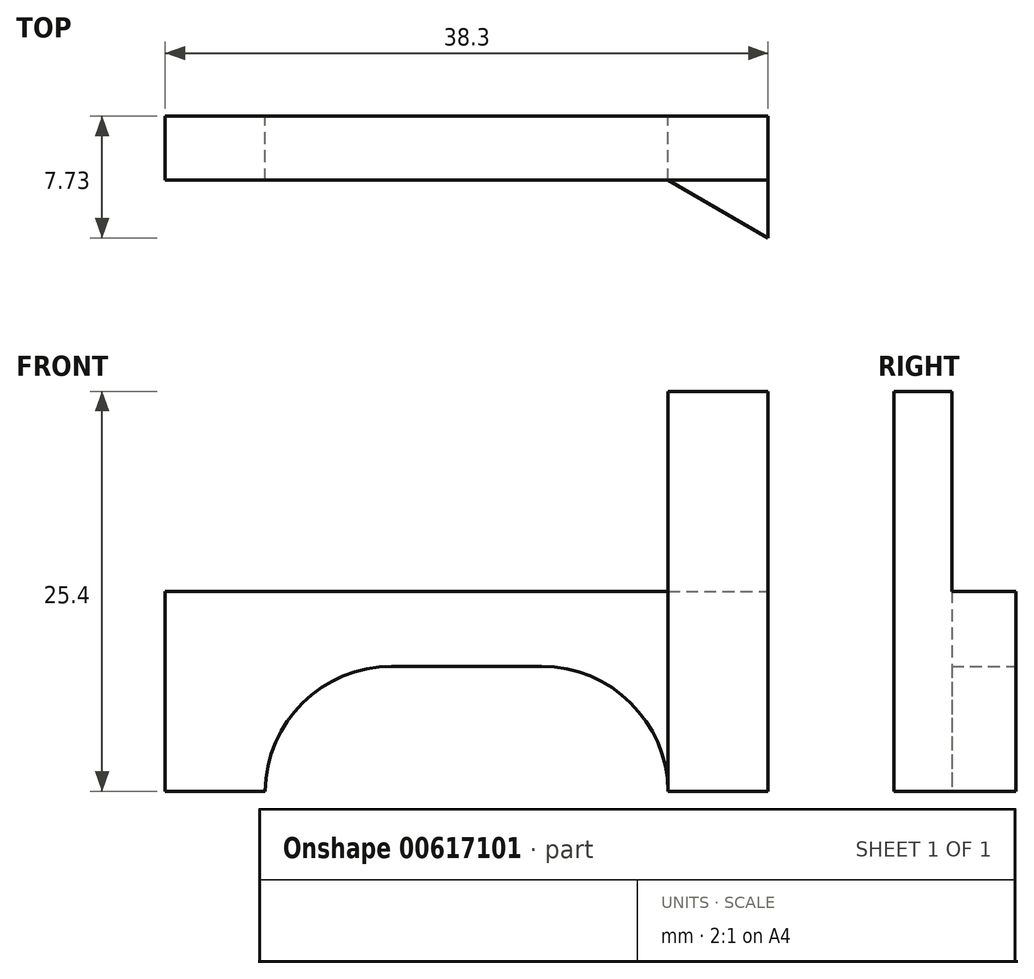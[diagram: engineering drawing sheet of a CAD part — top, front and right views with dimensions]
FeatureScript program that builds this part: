
annotation { "Feature Type Name" : "Feature", "Feature Type Description" : "" }
export const myFeature = defineFeature(function(context is Context, id is Id, definition is map)
    precondition{}
    {
        {
            var Q0;
            Q0=qCreatedBy(makeId("Front.planeOp"),FACE);
            var sketch = newSketch(context, id + "F0", { "sketchPlane" : qUnion([Q0])});
            skLineSegment(sketch, "E0", {"start": v(-31.85, -12.7) * mm, "end": v(-12.8, -12.7) * mm});
            skLineSegment(sketch, "E1", {"start": v(12.8, -12.7) * mm, "end": v(31.85, -12.7) * mm});
            skLineSegment(sketch, "E2", {"start": v(31.85, -12.7) * mm, "end": v(31.85, 0) * mm});
            skLineSegment(sketch, "E3", {"start": v(-4.76, -4.76) * mm, "end": v(0, -4.76) * mm});
            skArc(sketch, "E4", {"start": v(-4.76, -4.76) * mm, "mid": v(-10.4, -7.08) * mm, "end": v(-12.8, -12.7) * mm});
            skArc(sketch, "E5", {"start": v(12.8, -12.7) * mm, "mid": v(10.4, -7.08) * mm, "end": v(4.76, -4.76) * mm});
            skLineSegment(sketch, "E6", {"start": v(-31.85, 0) * mm, "end": v(-31.85, -12.7) * mm});
            skLineSegment(sketch, "E7", {"start": v(0, -4.76) * mm, "end": v(4.76, -4.76) * mm});
            skLineSegment(sketch, "E8", {"start": v(-31.85, 0) * mm, "end": v(0, 0) * mm});
            skLineSegment(sketch, "E9", {"start": v(0, 0) * mm, "end": v(31.85, 0) * mm});
            skSolve(sketch);
        }
        {
            var Q0;
            Q0=qSketchRegion(id+"F0",true);
            extrude(context, id + "F1", {"entities" : qUnion([Q0]), "flatOperationType" : FlatOperationType.REMOVE, "endBound" : BoundingType.SYMMETRIC, "depth" : 4.06 * mm, "offsetDistance" : 25.4 * mm, "domain" : OperationDomain.MODEL});
        }
        {
            var Q0;
            Q0=qCreatedBy(makeId("Top.planeOp"),FACE);
            var sketch = newSketch(context, id + "F2", { "sketchPlane" : qUnion([Q0])});
            skLineSegment(sketch, "E10", {"start": v(12.8, -2.03) * mm, "end": v(19.15, -5.7) * mm});
            skLineSegment(sketch, "E11", {"start": v(19.15, -5.7) * mm, "end": v(19.15, -2.03) * mm});
            skLineSegment(sketch, "E12", {"start": v(19.15, -2.03) * mm, "end": v(12.8, -2.03) * mm});
            skSolve(sketch);
        }
        {
            var Q0;
            Q0 = qSketchRegion(id + "F2", true);
            extrude(context, id + "F3", {"entities" : qUnion([Q0]), "operationType" : NewBodyOperationType.ADD, "flatOperationType" : FlatOperationType.REMOVE, "endBound" : BoundingType.SYMMETRIC, "depth" : 25.4 * mm, "offsetDistance" : 25.4 * mm, "domain" : OperationDomain.MODEL});
        }
        {
            var Q0;
            {var subQ0=sQuery(id+"F2.wireOp",EDGE,"E12");var subQ1=sQuery(id+"F2.wireOp",EDGE,"E11");var subQ2=sQuery(id+"F2.wireOp",EDGE,"E10");Q0=makeQuery(id+"F9uebhGRNWVXSQu_1.1.F3.boolean.opBoolean","MERGE",FACE,{"derivedFrom":[makeQuery(id+"F3.boolean.opBoolean","MERGE",FACE,{"derivedFrom":[makeQuery(id+"F1.opExtrude","SWEPT_FACE",FACE,{"disambiguationData":[OSD([sQuery(id+"F0.wireOp",EDGE,"E1")])]}),makeQuery(id+"F3.opExtrude","CAP_FACE",FACE,{"disambiguationData":[OSD([subQ2,subQ1,subQ0])],"isStart":true})]}),makeQuery(id+"F9uebhGRNWVXSQu_1.1.F3.opExtrude","CAP_FACE",FACE,{"disambiguationData":[OSD([subQ2,subQ1,subQ0])],"isStart":true})]});}
            var sketch = newSketch(context, id + "F4", { "sketchPlane" : qUnion([Q0])});
            skLineSegment(sketch, "E13.bottom", {"start": v(19.15, 2.03) * mm, "end": v(31.85, 2.03) * mm});
            skLineSegment(sketch, "E13.top", {"start": v(19.15, -2.03) * mm, "end": v(31.85, -2.03) * mm});
            skLineSegment(sketch, "E13.left", {"start": v(19.15, 2.03) * mm, "end": v(19.15, -2.03) * mm});
            skLineSegment(sketch, "E13.right", {"start": v(31.85, 2.03) * mm, "end": v(31.85, -2.03) * mm});
            skLineSegment(sketch, "E14.bottom", {"start": v(-19.15, -2.03) * mm, "end": v(-31.85, -2.03) * mm});
            skLineSegment(sketch, "E14.top", {"start": v(-19.15, 2.03) * mm, "end": v(-31.85, 2.03) * mm});
            skLineSegment(sketch, "E14.left", {"start": v(-19.15, -2.03) * mm, "end": v(-19.15, 2.03) * mm});
            skLineSegment(sketch, "E14.right", {"start": v(-31.85, -2.03) * mm, "end": v(-31.85, 2.03) * mm});
            skSolve(sketch);
        }
        {
            var Q0;
            Q0 = qSketchRegion(id + "F4", true);
            extrude(context, id + "F5", {"entities" : qUnion([Q0]), "operationType" : NewBodyOperationType.REMOVE, "oppositeDirection" : true, "depth" : 25.4 * mm, "offsetDistance" : 25.4 * mm});
        }
    });
